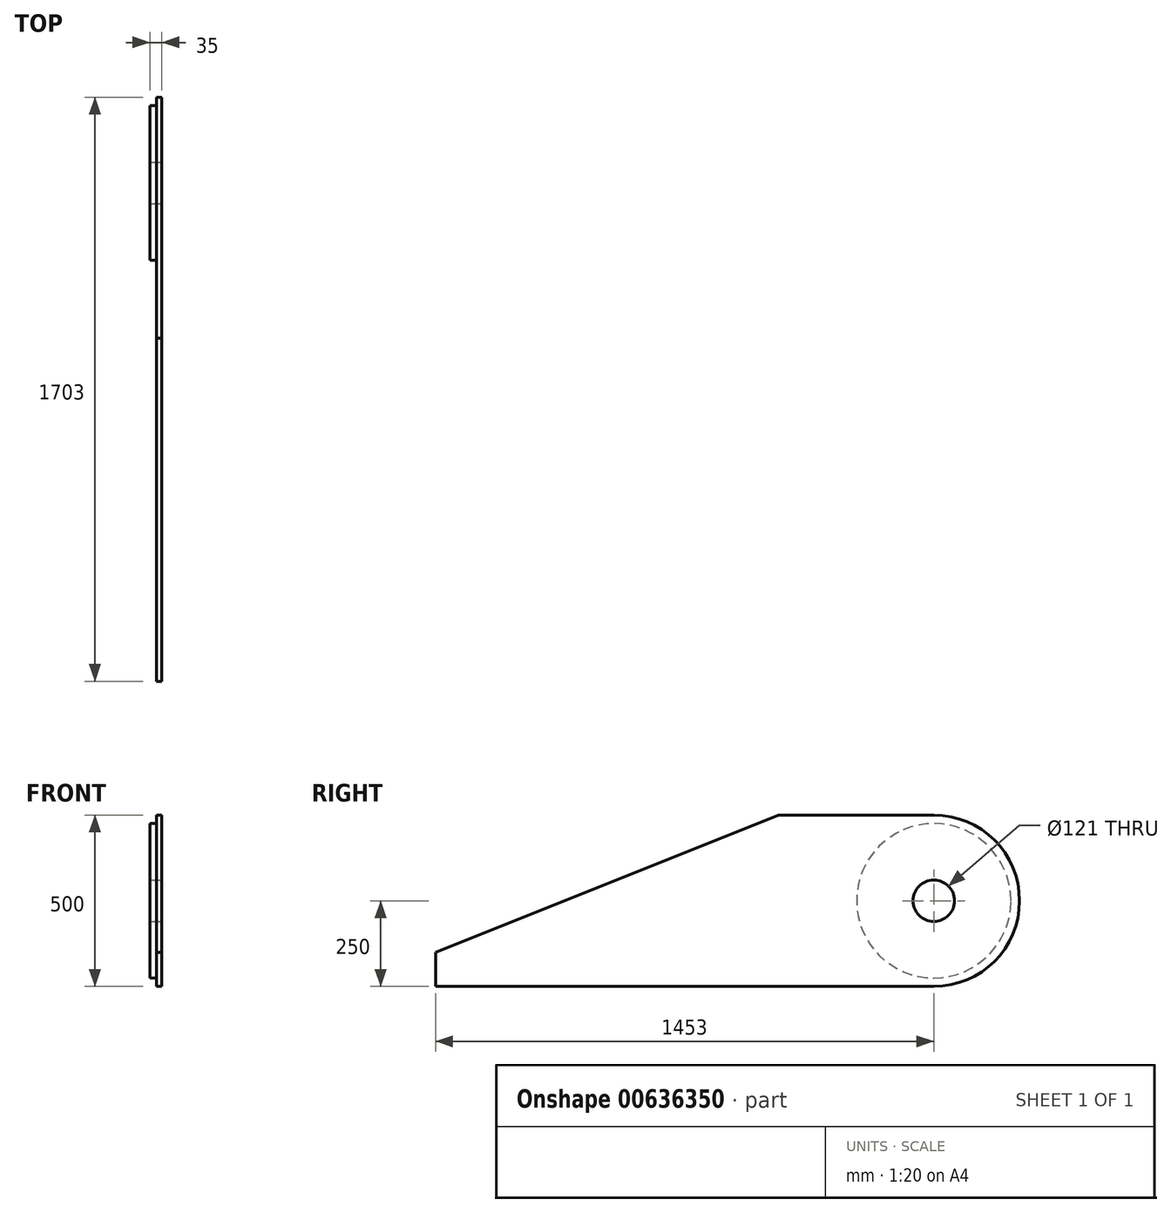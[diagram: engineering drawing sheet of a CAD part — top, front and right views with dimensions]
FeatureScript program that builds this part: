
annotation { "Feature Type Name" : "Feature", "Feature Type Description" : "" }
export const myFeature = defineFeature(function(context is Context, id is Id, definition is map)
    precondition{}
    {
        {
            var Q0;
            Q0=qCreatedBy(makeId("Right.planeOp"),FACE);
            var sketch = newSketch(context, id + "F0", { "sketchPlane" : qUnion([Q0])});
            skLineSegment(sketch, "E0", {"start": v(-726.5, 0) * mm, "end": v(726.5, 0) * mm});
            skLineSegment(sketch, "E1", {"start": v(-726.5, 0) * mm, "end": v(-726.5, 100) * mm});
            skLineSegment(sketch, "E2", {"start": v(-726.5, 100) * mm, "end": v(273.5, 500) * mm});
            skLineSegment(sketch, "E3", {"start": v(273.5, 500) * mm, "end": v(726.5, 500) * mm});
            skPoint(sketch, "E4", {"position": v(726.5, 250) * mm});
            skArc(sketch, "E5", {"start": v(726.5, 0) * mm, "mid": v(976.5, 250) * mm, "end": v(726.5, 500) * mm});
            skCircle(sketch, "E6", {"center": v(726.5, 250) * mm, "radius": 60.5 * mm});
            skCircle(sketch, "E7", {"center": v(726.5, 250) * mm, "radius": 225 * mm});
            skSolve(sketch);
        }
        {
            var Q0;
            Q0=makeQuery(id+"F0.imprint","IMPRINT",FACE,{"disambiguationData":[TD([[makeQuery(id+"F0.imprint","IMPRINT",EDGE,{"derivedFrom":sQuery(id+"F0.wireOp",EDGE,"E0")}),1.0]])]});
            var Q1;
            Q1=makeQuery(id+"F0.imprint","IMPRINT",FACE,{"disambiguationData":[TD([[makeQuery(id+"F0.imprint","IMPRINT",EDGE,{"derivedFrom":sQuery(id+"F0.wireOp",EDGE,"E6")}),-1.0]])]});
            extrude(context, id + "F1", {"entities" : qUnion([Q0, Q1]), "oppositeDirection" : true, "depth" : 15 * mm, "offsetDistance" : 25 * mm});
        }
        {
            var Q0;
            Q0=makeQuery(id+"F1.opExtrude","CAP_FACE",FACE,{"disambiguationData":[OSD([sQuery(id+"F0.wireOp",EDGE,"E0"),sQuery(id+"F0.wireOp",EDGE,"E1"),sQuery(id+"F0.wireOp",EDGE,"E2"),sQuery(id+"F0.wireOp",EDGE,"E3"),sQuery(id+"F0.wireOp",EDGE,"E5"),sQuery(id+"F0.wireOp",EDGE,"E6")])],"isStart":false});
            var sketch = newSketch(context, id + "F2", { "sketchPlane" : qUnion([Q0])});
            skCircle(sketch, "E8.0", {"center": v(-726.5, 250) * mm, "radius": 225 * mm});
            skCircle(sketch, "E9.0", {"center": v(-726.5, 250) * mm, "radius": 60.5 * mm});
            skCircle(sketch, "E9.1", {"center": v(-726.5, 250) * mm, "radius": 60.5 * mm});
            skSolve(sketch);
        }
        {
            var Q0;
            Q0=qSketchRegion(id+"F2",true);
            extrude(context, id + "F3", {"entities" : qUnion([Q0]), "operationType" : NewBodyOperationType.ADD, "depth" : 20 * mm, "offsetDistance" : 25 * mm});
        }
    });
